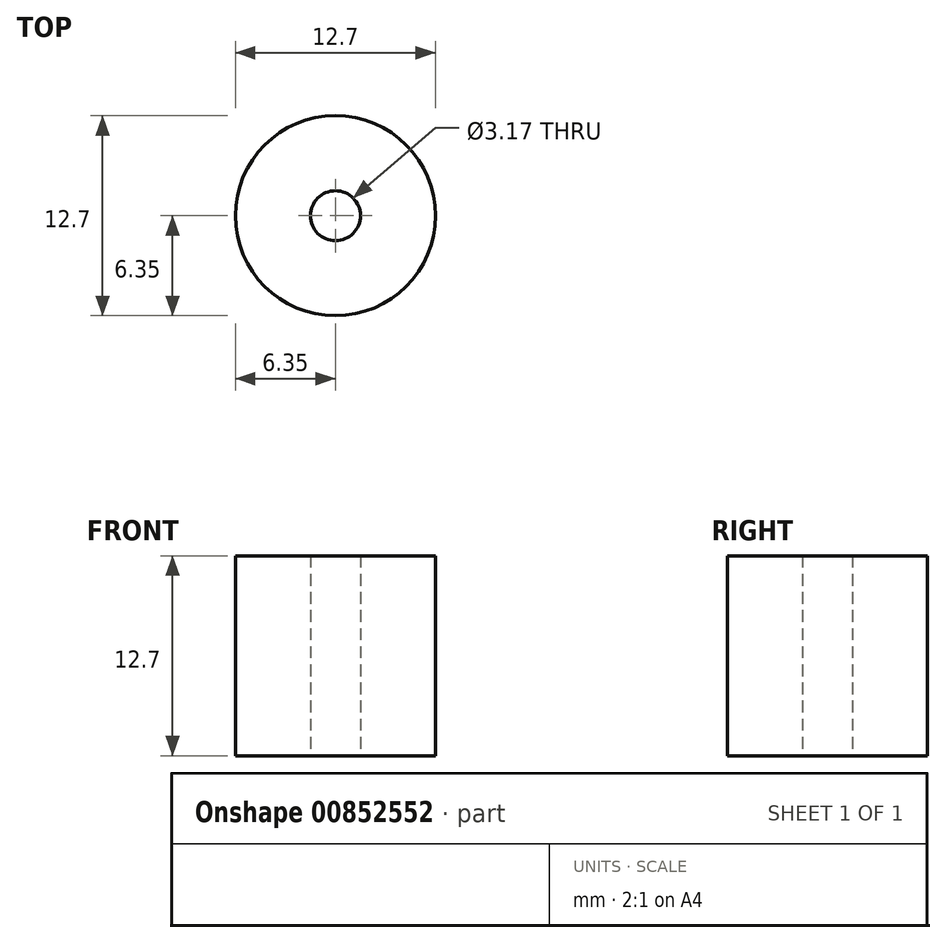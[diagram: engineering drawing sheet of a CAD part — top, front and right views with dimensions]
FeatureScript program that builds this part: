
annotation { "Feature Type Name" : "Feature", "Feature Type Description" : "" }
export const myFeature = defineFeature(function(context is Context, id is Id, definition is map)
    precondition{}
    {
        {
            var Q0;
            Q0=qCreatedBy(makeId("Top.planeOp"),FACE);
            var sketch = newSketch(context, id + "F0", { "sketchPlane" : qUnion([Q0])});
            skCircle(sketch, "E0", {"center": v(0, 0) * mm, "radius": 1.59 * mm});
            skCircle(sketch, "E1", {"center": v(0, 0) * mm, "radius": 6.35 * mm});
            skSolve(sketch);
        }
        {
            var Q0;
            Q0=qSketchRegion(id+"F0",true);
            extrude(context, id + "F1", {"entities" : qUnion([Q0]), "depth" : 12.7 * mm, "offsetDistance" : 25 * mm});
        }
    });
